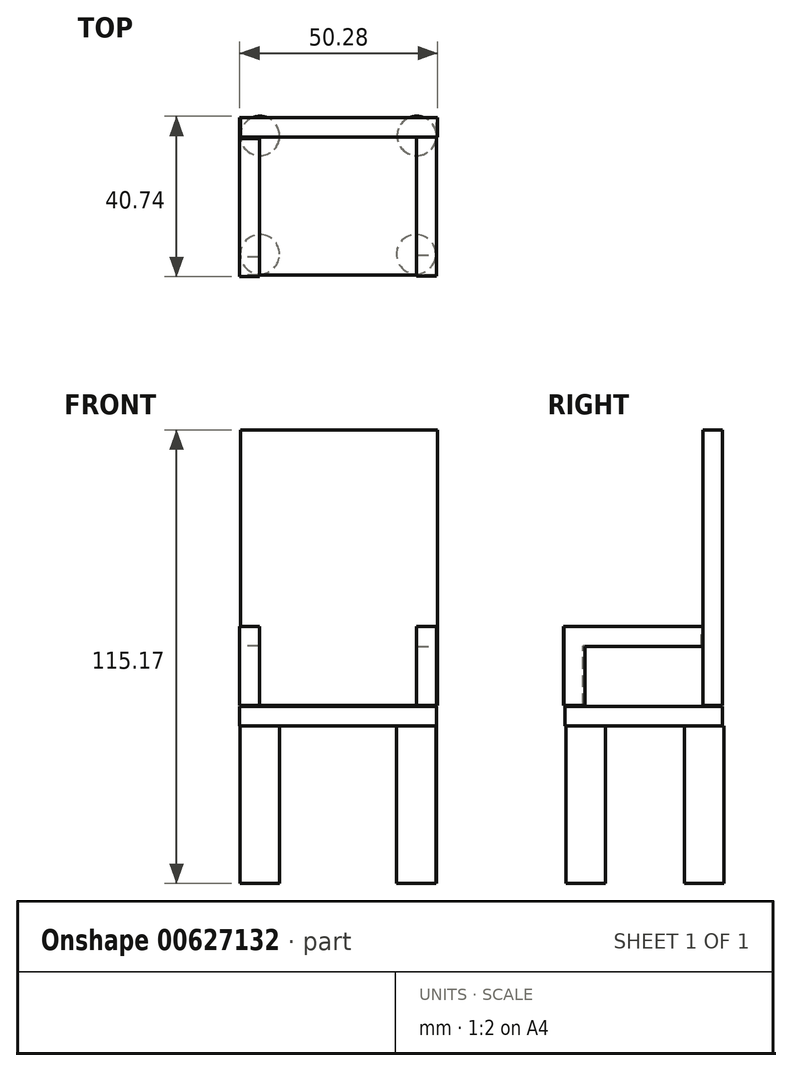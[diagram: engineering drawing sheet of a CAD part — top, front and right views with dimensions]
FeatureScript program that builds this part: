
annotation { "Feature Type Name" : "Feature", "Feature Type Description" : "" }
export const myFeature = defineFeature(function(context is Context, id is Id, definition is map)
    precondition{}
    {
        {
            var Q0;
            Q0=qCreatedBy(makeId("Top.planeOp"),FACE);
            var sketch = newSketch(context, id + "F0", { "sketchPlane" : qUnion([Q0])});
            skLineSegment(sketch, "E0.bottom", {"start": v(25, -20) * mm, "end": v(-25, -20) * mm});
            skLineSegment(sketch, "E0.top", {"start": v(25, 20) * mm, "end": v(-25, 20) * mm});
            skLineSegment(sketch, "E0.left", {"start": v(25, -20) * mm, "end": v(25, 20) * mm});
            skLineSegment(sketch, "E0.right", {"start": v(-25, -20) * mm, "end": v(-25, 20) * mm});
            skPoint(sketch, "E0.middle", {"position": v(0, 0) * mm});
            skSolve(sketch);
        }
        {
            var Q0;
            Q0=qCreatedBy(makeId("Top.planeOp"),FACE);
            var sketch = newSketch(context, id + "F1", { "sketchPlane" : qUnion([Q0])});
            skCircle(sketch, "E1", {"center": v(-19.83, 15.32) * mm, "radius": 5 * mm});
            skCircle(sketch, "E2", {"center": v(-19.83, -14.75) * mm, "radius": 5 * mm});
            skCircle(sketch, "E3", {"center": v(20.02, 15.32) * mm, "radius": 5 * mm});
            skCircle(sketch, "E4", {"center": v(19.83, -14.75) * mm, "radius": 5 * mm});
            skSolve(sketch);
        }
        {
            var Q0;
            Q0=qSketchRegion(id+"F1",true);
            extrude(context, id + "F2", {"entities" : qUnion([Q0]), "oppositeDirection" : true, "depth" : 40 * mm, "offsetDistance" : 25 * mm});
        }
        {
            var Q0;
            Q0=makeQuery(id+"F0.imprint","IMPRINT",FACE,{"disambiguationData":[TD([[makeQuery(id+"F0.imprint","IMPRINT",EDGE,{"derivedFrom":sQuery(id+"F0.wireOp",EDGE,"E0.bottom")}),-1.0]])]});
            extrude(context, id + "F3", {"entities" : qUnion([Q0]), "operationType" : NewBodyOperationType.ADD, "depth" : 5 * mm, "offsetDistance" : 25 * mm});
        }
        {
            var Q0;
            Q0=qCreatedBy(makeId("Front.planeOp"),FACE);
            cPlane(context, id + "F4", {"entities" : qUnion([Q0]), "cplaneType" : CPlaneType.OFFSET, "offset" : 20 * mm, "oppositeDirection" : true, "width" : 150 * mm, "height" : 150 * mm});
        }
        {
            var Q0;
            Q0=qCreatedBy(id+"F4.planeOp",FACE);
            var sketch = newSketch(context, id + "F5", { "sketchPlane" : qUnion([Q0])});
            skLineSegment(sketch, "E5.bottom", {"start": v(-24.72, 5.17) * mm, "end": v(25.28, 5.17) * mm});
            skLineSegment(sketch, "E5.top", {"start": v(-24.72, 75.17) * mm, "end": v(25.28, 75.17) * mm});
            skLineSegment(sketch, "E5.left", {"start": v(-24.72, 5.17) * mm, "end": v(-24.72, 75.17) * mm});
            skLineSegment(sketch, "E5.right", {"start": v(25.28, 5.17) * mm, "end": v(25.28, 75.17) * mm});
            skSolve(sketch);
        }
        {
            var Q0;
            Q0=makeQuery(id+"F5.imprint","IMPRINT",FACE,{"disambiguationData":[TD([[makeQuery(id+"F5.imprint","IMPRINT",EDGE,{"derivedFrom":sQuery(id+"F5.wireOp",EDGE,"E5.bottom")}),1.0]])]});
            extrude(context, id + "F6", {"entities" : qUnion([Q0]), "operationType" : NewBodyOperationType.ADD, "depth" : 5 * mm, "offsetDistance" : 25 * mm});
        }
        {
            var Q0;
            Q0=qCreatedBy(makeId("Right.planeOp"),FACE);
            cPlane(context, id + "F7", {"entities" : qUnion([Q0]), "cplaneType" : CPlaneType.OFFSET, "offset" : 25 * mm, "width" : 150 * mm, "height" : 150 * mm});
        }
        {
            var Q0;
            Q0=qCreatedBy(makeId("Right.planeOp"),FACE);
            cPlane(context, id + "F8", {"entities" : qUnion([Q0]), "cplaneType" : CPlaneType.OFFSET, "offset" : 25 * mm, "oppositeDirection" : true, "width" : 150 * mm, "height" : 150 * mm});
        }
        {
            var Q0;
            Q0=qCreatedBy(id+"F7.planeOp",FACE);
            var sketch = newSketch(context, id + "F9", { "sketchPlane" : qUnion([Q0])});
            skLineSegment(sketch, "E6.bottom", {"start": v(19.7, 5.2) * mm, "end": v(-20.3, 5.2) * mm});
            skLineSegment(sketch, "E6.top", {"start": v(19.7, 25.2) * mm, "end": v(-20.3, 25.2) * mm});
            skLineSegment(sketch, "E6.left", {"start": v(19.7, 5.2) * mm, "end": v(19.7, 25.2) * mm});
            skLineSegment(sketch, "E6.right", {"start": v(-20.3, 5.2) * mm, "end": v(-20.3, 25.2) * mm});
            skSolve(sketch);
        }
        {
            var Q0;
            Q0=makeQuery(id+"F9.imprint","IMPRINT",FACE,{"disambiguationData":[TD([[makeQuery(id+"F9.imprint","IMPRINT",EDGE,{"derivedFrom":sQuery(id+"F9.wireOp",EDGE,"E6.bottom")}),-1.0]])]});
            extrude(context, id + "F10", {"entities" : qUnion([Q0]), "operationType" : NewBodyOperationType.ADD, "oppositeDirection" : true, "depth" : 5 * mm, "offsetDistance" : 25 * mm});
        }
        {
            var Q0;
            Q0=makeQuery(id+"F10.opExtrude","CAP_FACE",FACE,{"disambiguationData":[OSD([sQuery(id+"F9.wireOp",EDGE,"E6.bottom"),sQuery(id+"F9.wireOp",EDGE,"E6.top"),sQuery(id+"F9.wireOp",EDGE,"E6.left"),sQuery(id+"F9.wireOp",EDGE,"E6.right")])],"isStart":true});
            var sketch = newSketch(context, id + "F11", { "sketchPlane" : qUnion([Q0])});
            skLineSegment(sketch, "E7.bottom", {"start": v(15, 5.2) * mm, "end": v(-15, 5.2) * mm});
            skLineSegment(sketch, "E7.top", {"start": v(15, 20.2) * mm, "end": v(-15, 20.2) * mm});
            skLineSegment(sketch, "E7.left", {"start": v(15, 5.2) * mm, "end": v(15, 20.2) * mm});
            skLineSegment(sketch, "E7.right", {"start": v(-15, 5.2) * mm, "end": v(-15, 20.2) * mm});
            skSolve(sketch);
        }
        {
            var Q0;
            Q0=makeQuery(id+"F11.imprint","IMPRINT",FACE,{"disambiguationData":[TD([[makeQuery(id+"F11.imprint","IMPRINT",EDGE,{"derivedFrom":sQuery(id+"F11.wireOp",EDGE,"E7.bottom")}),-1.0]])]});
            extrude(context, id + "F12", {"entities" : qUnion([Q0]), "operationType" : NewBodyOperationType.REMOVE, "oppositeDirection" : true, "depth" : 5 * mm, "offsetDistance" : 25 * mm});
        }
        {
            var Q0;
            Q0=qCreatedBy(id+"F8.planeOp",FACE);
            var sketch = newSketch(context, id + "F13", { "sketchPlane" : qUnion([Q0])});
            skLineSegment(sketch, "E8.bottom", {"start": v(14.58, 5.26) * mm, "end": v(-20.42, 5.26) * mm});
            skLineSegment(sketch, "E8.top", {"start": v(14.58, 25.26) * mm, "end": v(-20.42, 25.26) * mm});
            skLineSegment(sketch, "E8.left", {"start": v(14.58, 5.26) * mm, "end": v(14.58, 25.26) * mm});
            skLineSegment(sketch, "E8.right", {"start": v(-20.42, 5.26) * mm, "end": v(-20.42, 25.26) * mm});
            skSolve(sketch);
        }
        {
            var Q0;
            Q0=makeQuery(id+"F13.imprint","IMPRINT",FACE,{"disambiguationData":[TD([[makeQuery(id+"F13.imprint","IMPRINT",EDGE,{"derivedFrom":sQuery(id+"F13.wireOp",EDGE,"E8.bottom")}),-1.0]])]});
            extrude(context, id + "F14", {"entities" : qUnion([Q0]), "operationType" : NewBodyOperationType.ADD, "depth" : 5 * mm, "offsetDistance" : 25 * mm});
        }
        {
            var Q0;
            Q0=makeQuery(id+"F14.opExtrude","CAP_FACE",FACE,{"disambiguationData":[OSD([sQuery(id+"F13.wireOp",EDGE,"E8.bottom"),sQuery(id+"F13.wireOp",EDGE,"E8.top"),sQuery(id+"F13.wireOp",EDGE,"E8.left"),sQuery(id+"F13.wireOp",EDGE,"E8.right")])],"isStart":true});
            var sketch = newSketch(context, id + "F15", { "sketchPlane" : qUnion([Q0])});
            skLineSegment(sketch, "E9.bottom", {"start": v(-14.58, 5.26) * mm, "end": v(15.42, 5.26) * mm});
            skLineSegment(sketch, "E9.top", {"start": v(-14.58, 20.26) * mm, "end": v(15.42, 20.26) * mm});
            skLineSegment(sketch, "E9.left", {"start": v(-14.58, 5.26) * mm, "end": v(-14.58, 20.26) * mm});
            skLineSegment(sketch, "E9.right", {"start": v(15.42, 5.26) * mm, "end": v(15.42, 20.26) * mm});
            skSolve(sketch);
        }
        {
            var Q0;
            Q0=makeQuery(id+"F15.imprint","IMPRINT",FACE,{"disambiguationData":[TD([[makeQuery(id+"F15.imprint","IMPRINT",EDGE,{"derivedFrom":sQuery(id+"F15.wireOp",EDGE,"E9.bottom")}),1.0]])]});
            extrude(context, id + "F16", {"entities" : qUnion([Q0]), "operationType" : NewBodyOperationType.REMOVE, "oppositeDirection" : true, "depth" : 5 * mm, "offsetDistance" : 25 * mm});
        }
    });
